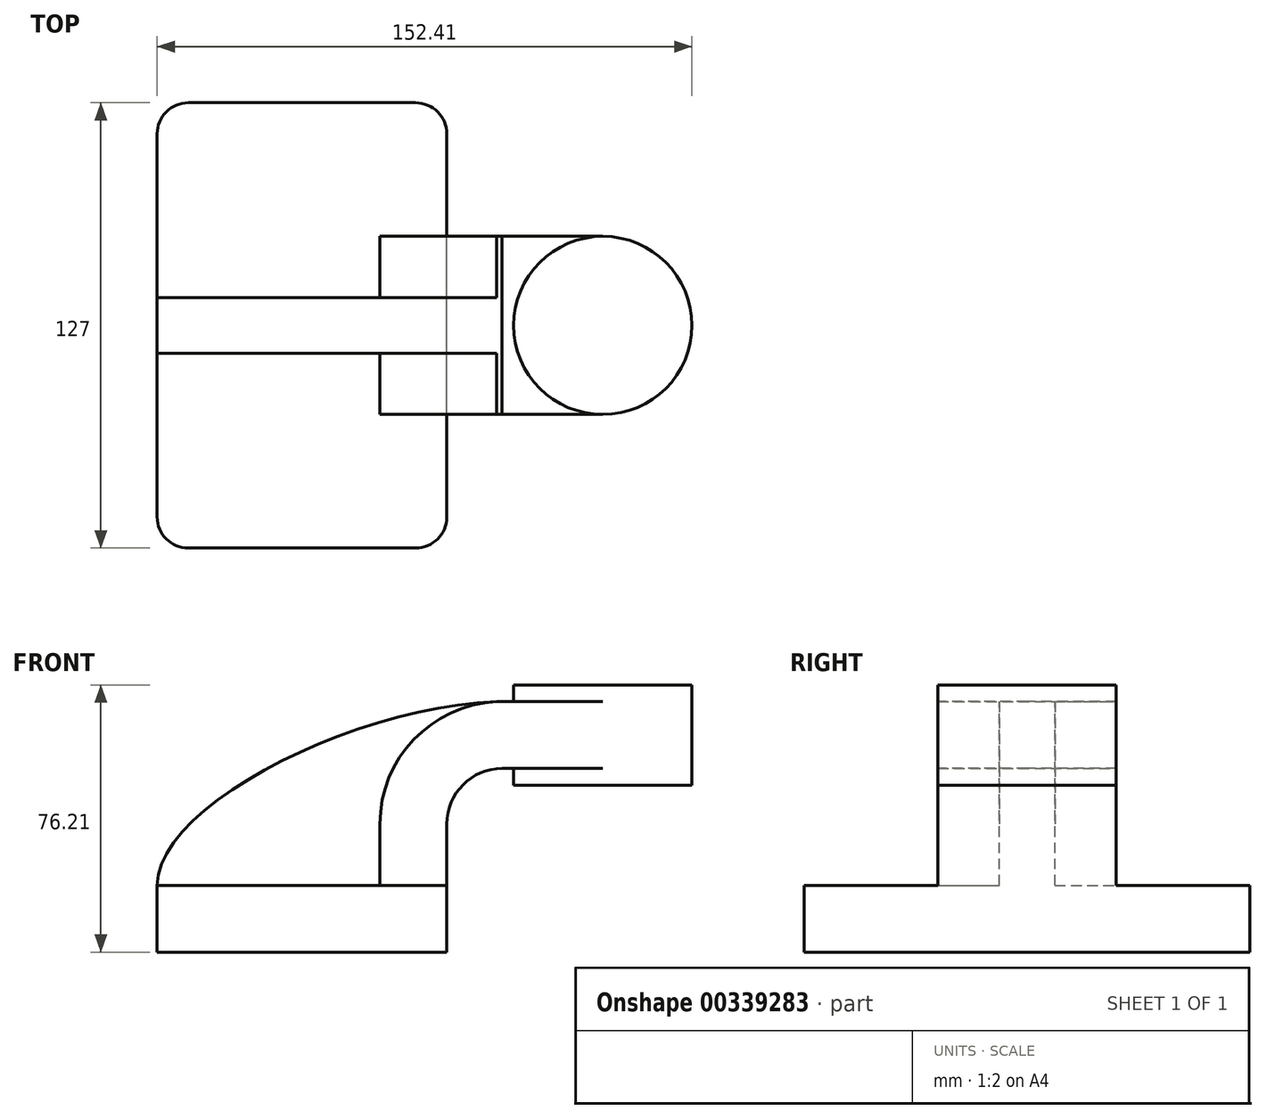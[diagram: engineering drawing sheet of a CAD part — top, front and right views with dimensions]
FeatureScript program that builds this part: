
annotation { "Feature Type Name" : "Feature", "Feature Type Description" : "" }
export const myFeature = defineFeature(function(context is Context, id is Id, definition is map)
    precondition{}
    {
        {
            var Q0;
            Q0=qCreatedBy(makeId("Front.planeOp"),FACE);
            var sketch = newSketch(context, id + "F0", { "sketchPlane" : qUnion([Q0])});
            skLineSegment(sketch, "E0.bottom", {"start": v(-41.28, -9.52) * mm, "end": v(41.28, -9.52) * mm});
            skLineSegment(sketch, "E0.top", {"start": v(-41.28, 9.52) * mm, "end": v(41.27, 9.52) * mm});
            skLineSegment(sketch, "E0.left", {"start": v(-41.27, -9.52) * mm, "end": v(-41.28, 9.52) * mm});
            skLineSegment(sketch, "E0.right", {"start": v(41.28, -9.52) * mm, "end": v(41.27, 9.52) * mm});
            skPoint(sketch, "E0.middle", {"position": v(0, 0) * mm});
            skLineSegment(sketch, "E1.bottom", {"start": v(60.32, 38.1) * mm, "end": v(111.12, 38.1) * mm});
            skLineSegment(sketch, "E1.top", {"start": v(60.32, 66.68) * mm, "end": v(111.12, 66.68) * mm});
            skLineSegment(sketch, "E1.left", {"start": v(60.32, 38.1) * mm, "end": v(60.32, 66.68) * mm});
            skLineSegment(sketch, "E1.right", {"start": v(111.13, 38.1) * mm, "end": v(111.12, 66.68) * mm});
            skPoint(sketch, "E1.middle", {"position": v(85.72, 52.39) * mm});
            skLineSegment(sketch, "E2", {"start": v(41.27, 9.52) * mm, "end": v(41.27, 27) * mm});
            skArc(sketch, "E3", {"start": v(41.27, 27) * mm, "mid": v(45.89, 38.19) * mm, "end": v(57.05, 42.88) * mm});
            skLineSegment(sketch, "E4", {"start": v(57.05, 42.88) * mm, "end": v(85.72, 42.88) * mm});
            skLineSegment(sketch, "E5.0", {"start": v(57, 61.93) * mm, "end": v(85.72, 61.93) * mm});
            skArc(sketch, "E5.1", {"start": v(22.23, 27) * mm, "mid": v(32.4, 51.64) * mm, "end": v(57, 61.93) * mm});
            skLineSegment(sketch, "E5.2", {"start": v(22.22, 9.52) * mm, "end": v(22.22, 27) * mm});
            skLineSegment(sketch, "E6", {"start": v(85.72, 38.1) * mm, "end": v(85.72, 66.68) * mm});
            skFitSpline(sketch, "E7", {"points": [v(-41.28, 9.53) * mm, v(57, 61.93) * mm], "startDerivative": vector(0.32, 69.09) * mm, "endDerivative": vector(123.69, 2.28) * mm});
            skSolve(sketch);
        }
        {
            var Q0;
            Q0=makeQuery(id+"F0.imprint","IMPRINT",FACE,{"disambiguationData":[TD([[makeQuery(id+"F0.imprint","IMPRINT",EDGE,{"derivedFrom":sQuery(id+"F0.wireOp",EDGE,"E0.bottom")}),1.0]])]});
            extrude(context, id + "F1", {"entities" : qUnion([Q0]), "endBound" : BoundingType.SYMMETRIC, "depth" : 127 * mm});
        }
        {
            var Q0;
            {var subQ0=sQuery(id+"F0.wireOp",EDGE,"E4");var subQ1=sQuery(id+"F0.wireOp",EDGE,"E1.left");var subQ2=makeQuery(id+"F0.imprint","INTERSECT",VERTEX,{"derivedFrom":[subQ1,subQ0]});Q0=makeQuery(id+"F0.imprint","IMPRINT",FACE,{"disambiguationData":[TD([[makeQuery(id+"F0.imprint","IMPRINT",EDGE,{"disambiguationData":[TD([[subQ2,-1.0]])],"derivedFrom":subQ1}),-1.0]])]});}
            var Q1;
            {var subQ1=sQuery(id+"F0.wireOp",EDGE,"E2");Q1=makeQuery(id+"F0.imprint","IMPRINT",FACE,{"disambiguationData":[TD([[makeQuery(id+"F0.imprint","IMPRINT",EDGE,{"derivedFrom":subQ1}),1.0]])]});}
            extrude(context, id + "F2", {"entities" : qUnion([Q0, Q1]), "operationType" : NewBodyOperationType.ADD, "endBound" : BoundingType.SYMMETRIC, "depth" : 50.8 * mm});
        }
        {
            var Q0;
            {var subQ3=sQuery(id+"F0.wireOp",EDGE,"E5.2");Q0=makeQuery(id+"F0.imprint","IMPRINT",FACE,{"disambiguationData":[TD([[makeQuery(id+"F0.imprint","IMPRINT",EDGE,{"derivedFrom":subQ3}),1.0]])]});}
            extrude(context, id + "F3", {"entities" : qUnion([Q0]), "operationType" : NewBodyOperationType.ADD, "endBound" : BoundingType.SYMMETRIC, "depth" : 15.88 * mm});
        }
        {
            var Q0;
            {var subQ4=sQuery(id+"F0.wireOp",EDGE,"E1.right");Q0=makeQuery(id+"F0.imprint","IMPRINT",FACE,{"disambiguationData":[TD([[makeQuery(id+"F0.imprint","IMPRINT",EDGE,{"derivedFrom":subQ4}),1.0]])]});}
            var Q1;
            Q1=sQuery(id+"F0.wireOp",EDGE,"E6");
            revolve(context, id + "F4", {"operationType" : NewBodyOperationType.ADD, "entities" : qUnion([Q0]), "axis" : qUnion([Q1]), "revolveType" : RevolveType.FULL});
        }
        {
            var Q0;
            Q0=makeQuery(id+"F1.opExtrude","CAP_EDGE",EDGE,{"disambiguationData":[OSD([sQuery(id+"F0.wireOp",EDGE,"E0.left")])],"isStart":false});
            var Q1;
            Q1=makeQuery(id+"F1.opExtrude","CAP_EDGE",EDGE,{"disambiguationData":[OSD([sQuery(id+"F0.wireOp",EDGE,"E0.right")])],"isStart":false});
            var Q2;
            Q2=makeQuery(id+"F1.opExtrude","CAP_EDGE",EDGE,{"disambiguationData":[OSD([sQuery(id+"F0.wireOp",EDGE,"E0.right")])],"isStart":true});
            var Q3;
            Q3=makeQuery(id+"F1.opExtrude","CAP_EDGE",EDGE,{"disambiguationData":[OSD([sQuery(id+"F0.wireOp",EDGE,"E0.left")])],"isStart":true});
            fillet(context, id + "F5", {"entities" : qUnion([Q0, Q1, Q2, Q3]), "radius" : 8.9 * mm, "tangentPropagation" : true, "allowEdgeOverflow" : false});
        }
    });
